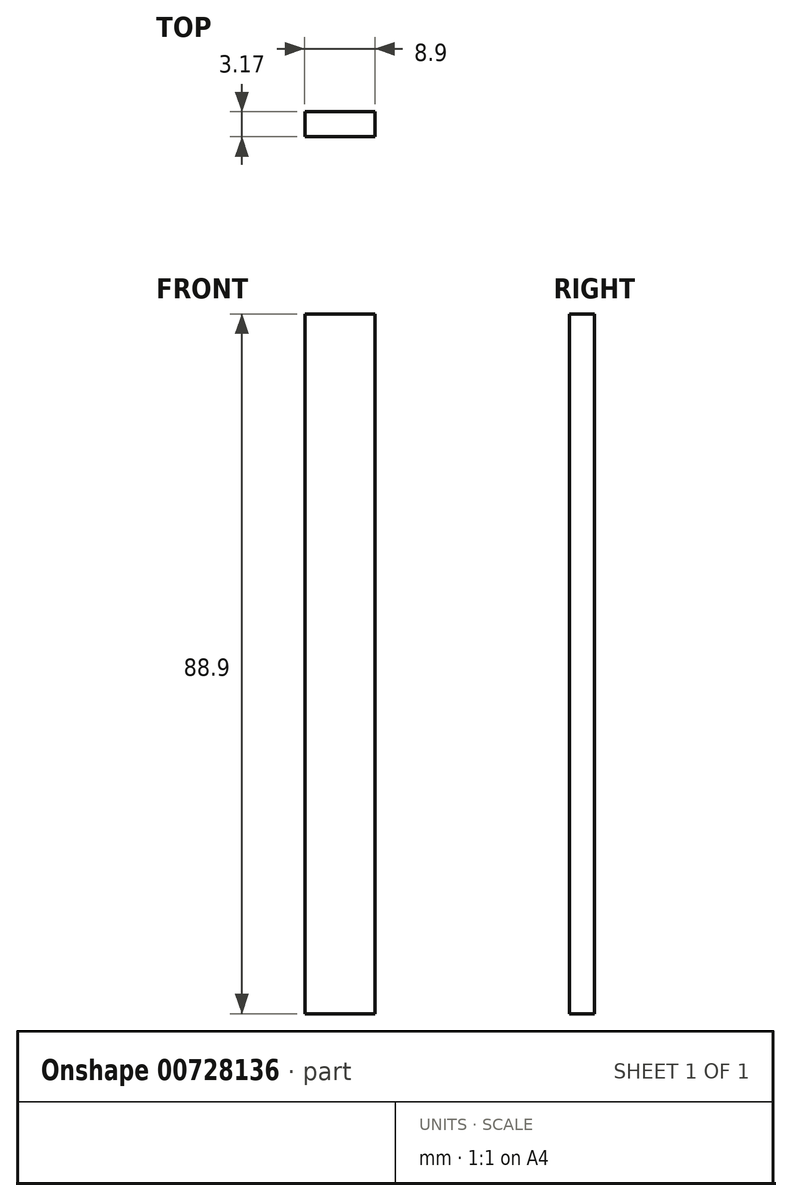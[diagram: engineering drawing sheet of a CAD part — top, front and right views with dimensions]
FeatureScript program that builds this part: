
annotation { "Feature Type Name" : "Feature", "Feature Type Description" : "" }
export const myFeature = defineFeature(function(context is Context, id is Id, definition is map)
    precondition{}
    {
        {
            var Q0;
            Q0=qCreatedBy(makeId("Front.planeOp"),FACE);
            var sketch = newSketch(context, id + "F0", { "sketchPlane" : qUnion([Q0])});
            skLineSegment(sketch, "E0.bottom", {"start": v(4.45, 44.45) * mm, "end": v(-4.44, 44.45) * mm});
            skLineSegment(sketch, "E0.top", {"start": v(4.44, -44.45) * mm, "end": v(-4.45, -44.45) * mm});
            skLineSegment(sketch, "E0.left", {"start": v(4.45, 44.45) * mm, "end": v(4.44, -44.45) * mm});
            skLineSegment(sketch, "E0.right", {"start": v(-4.44, 44.45) * mm, "end": v(-4.45, -44.45) * mm});
            skPoint(sketch, "E0.middle", {"position": v(0, 0) * mm});
            skSolve(sketch);
        }
        {
            var Q0;
            Q0=qSketchRegion(id+"F0",true);
            extrude(context, id + "F1", {"entities" : qUnion([Q0]), "depth" : 3.17 * mm, "offsetDistance" : 25.4 * mm});
        }
    });
